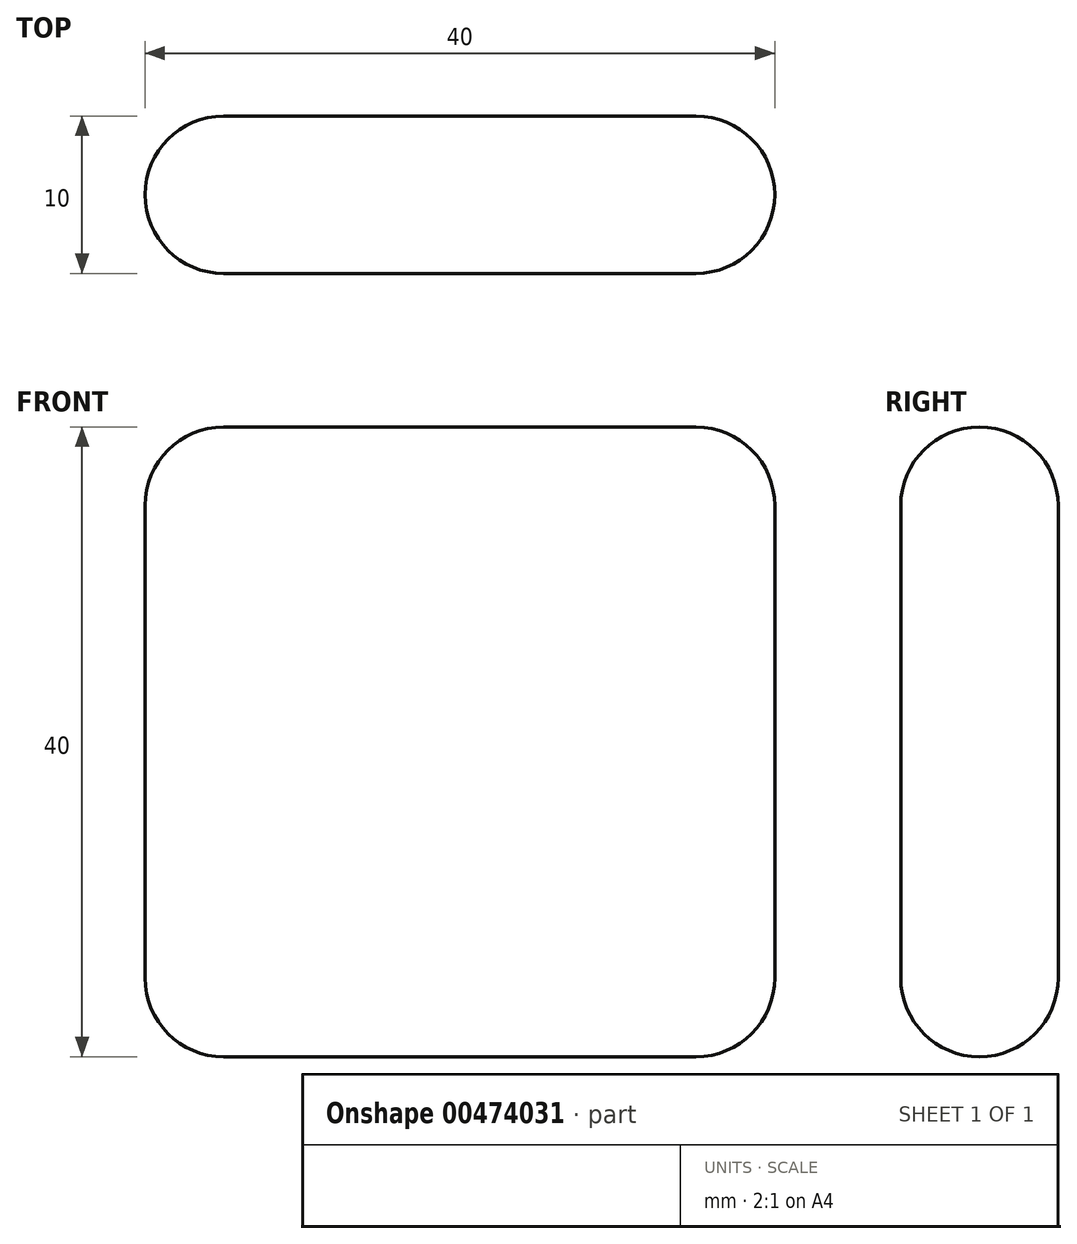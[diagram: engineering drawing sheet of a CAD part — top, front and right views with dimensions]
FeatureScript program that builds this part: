
annotation { "Feature Type Name" : "Feature", "Feature Type Description" : "" }
export const myFeature = defineFeature(function(context is Context, id is Id, definition is map)
    precondition{}
    {
        {
            var Q0;
            Q0=qCreatedBy(makeId("Front.planeOp"),FACE);
            var sketch = newSketch(context, id + "F0", { "sketchPlane" : qUnion([Q0])});
            skLineSegment(sketch, "E0.bottom", {"start": v(-19.76, 20.34) * mm, "end": v(20.24, 20.34) * mm});
            skLineSegment(sketch, "E0.top", {"start": v(-19.76, -19.66) * mm, "end": v(20.24, -19.66) * mm});
            skLineSegment(sketch, "E0.left", {"start": v(-19.76, 20.34) * mm, "end": v(-19.76, -19.66) * mm});
            skLineSegment(sketch, "E0.right", {"start": v(20.24, 20.34) * mm, "end": v(20.24, -19.66) * mm});
            skSolve(sketch);
        }
        {
            var Q0;
            Q0=makeQuery(id+"F0.imprint","IMPRINT",FACE,{"disambiguationData":[TD([[makeQuery(id+"F0.imprint","IMPRINT",EDGE,{"derivedFrom":sQuery(id+"F0.wireOp",EDGE,"E0.bottom")}),-1.0]])]});
            var sketch = newSketch(context, id + "F1", { "sketchPlane" : qUnion([Q0])});
            skSolve(sketch);
        }
        {
            var Q0;
            Q0=makeQuery(id+"F1.imprint","IMPRINT",FACE,{"disambiguationData":[TD([[makeQuery(id+"F1.imprint","IMPRINT",EDGE,{"derivedFrom":makeQuery(id+"F0.imprint","IMPRINT",EDGE,{"derivedFrom":sQuery(id+"F0.wireOp",EDGE,"E0.bottom")})}),-1.0]])]});
            var Q1;
            Q1=makeQuery(id+"F0.imprint","IMPRINT",FACE,{"disambiguationData":[TD([[makeQuery(id+"F0.imprint","IMPRINT",EDGE,{"derivedFrom":sQuery(id+"F0.wireOp",EDGE,"E0.bottom")}),-1.0]])]});
            extrude(context, id + "F2", {"entities" : qUnion([Q0, Q1]), "depth" : 10 * mm});
        }
        {
            var Q0;
            {var subQ0=sQuery(id+"F0.wireOp",EDGE,"E0.left");Q0=makeQuery(id+"F2.opExtrude","SWEPT_FACE",FACE,{"disambiguationData":[OSD([subQ0]),TDD([makeQuery(id+"F0.imprint","IMPRINT",EDGE,{"derivedFrom":subQ0})])]});}
            var Q1;
            {var subQ0=sQuery(id+"F0.wireOp",EDGE,"E0.right");Q1=makeQuery(id+"F2.opExtrude","SWEPT_FACE",FACE,{"disambiguationData":[OSD([subQ0]),TDD([makeQuery(id+"F0.imprint","IMPRINT",EDGE,{"derivedFrom":subQ0})])]});}
            var Q2;
            {var subQ0=sQuery(id+"F0.wireOp",EDGE,"E0.bottom");Q2=makeQuery(id+"F2.opExtrude","CAP_EDGE",EDGE,{"disambiguationData":[OSD([subQ0]),TDD([makeQuery(id+"F0.imprint","IMPRINT",EDGE,{"derivedFrom":subQ0})])],"isStart":true});}
            var Q3;
            {var subQ0=sQuery(id+"F0.wireOp",EDGE,"E0.bottom");Q3=makeQuery(id+"F2.opExtrude","CAP_EDGE",EDGE,{"disambiguationData":[OSD([subQ0]),TDD([makeQuery(id+"F0.imprint","IMPRINT",EDGE,{"derivedFrom":subQ0})])],"isStart":false});}
            var Q4;
            {var subQ0=sQuery(id+"F0.wireOp",EDGE,"E0.right");var subQ1=sQuery(id+"F0.wireOp",EDGE,"E0.bottom");Q4=makeQuery(id+"F2.opExtrude","SWEPT_EDGE",EDGE,{"disambiguationData":[OSD([subQ1,subQ0]),TDD([makeQuery(id+"F0.imprint","INTERSECT",VERTEX,{"derivedFrom":[subQ1,subQ0]})])]});}
            var Q5;
            {var subQ0=sQuery(id+"F0.wireOp",EDGE,"E0.right");var subQ1=sQuery(id+"F0.wireOp",EDGE,"E0.left");var subQ2=sQuery(id+"F0.wireOp",EDGE,"E0.top");var subQ3=sQuery(id+"F0.wireOp",EDGE,"E0.bottom");Q5=makeQuery(id+"F2.opExtrude","CAP_FACE",FACE,{"disambiguationData":[OSD([subQ3,subQ2,subQ1,subQ0]),TDD([makeQuery(id+"F0.imprint","IMPRINT",EDGE,{"derivedFrom":subQ3}),makeQuery(id+"F0.imprint","IMPRINT",EDGE,{"derivedFrom":subQ2}),makeQuery(id+"F0.imprint","IMPRINT",EDGE,{"derivedFrom":subQ1}),makeQuery(id+"F0.imprint","IMPRINT",EDGE,{"derivedFrom":subQ0})])],"isStart":true});}
            var Q6;
            {var subQ0=sQuery(id+"F0.wireOp",EDGE,"E0.left");var subQ1=sQuery(id+"F0.wireOp",EDGE,"E0.bottom");Q6=makeQuery(id+"F2.opExtrude","SWEPT_EDGE",EDGE,{"disambiguationData":[OSD([subQ1,subQ0]),TDD([makeQuery(id+"F0.imprint","INTERSECT",VERTEX,{"derivedFrom":[subQ1,subQ0]})])]});}
            var Q7;
            {var subQ0=sQuery(id+"F0.wireOp",EDGE,"E0.bottom");Q7=makeQuery(id+"F2.opExtrude","SWEPT_FACE",FACE,{"disambiguationData":[OSD([subQ0]),TDD([makeQuery(id+"F0.imprint","IMPRINT",EDGE,{"derivedFrom":subQ0})])]});}
            var Q8;
            {var subQ0=sQuery(id+"F0.wireOp",EDGE,"E0.right");var subQ1=sQuery(id+"F0.wireOp",EDGE,"E0.left");var subQ2=sQuery(id+"F0.wireOp",EDGE,"E0.top");var subQ3=sQuery(id+"F0.wireOp",EDGE,"E0.bottom");Q8=makeQuery(id+"F2.opExtrude","CAP_FACE",FACE,{"disambiguationData":[OSD([subQ3,subQ2,subQ1,subQ0]),TDD([makeQuery(id+"F0.imprint","IMPRINT",EDGE,{"derivedFrom":subQ3}),makeQuery(id+"F0.imprint","IMPRINT",EDGE,{"derivedFrom":subQ2}),makeQuery(id+"F0.imprint","IMPRINT",EDGE,{"derivedFrom":subQ1}),makeQuery(id+"F0.imprint","IMPRINT",EDGE,{"derivedFrom":subQ0})])],"isStart":false});}
            var Q9;
            {var subQ0=sQuery(id+"F0.wireOp",EDGE,"E0.right");var subQ1=sQuery(id+"F0.wireOp",EDGE,"E0.top");Q9=makeQuery(id+"F2.opExtrude","SWEPT_EDGE",EDGE,{"disambiguationData":[OSD([subQ1,subQ0]),TDD([makeQuery(id+"F0.imprint","INTERSECT",VERTEX,{"derivedFrom":[subQ1,subQ0]})])]});}
            var Q10;
            {var subQ0=sQuery(id+"F0.wireOp",EDGE,"E0.top");Q10=makeQuery(id+"F2.opExtrude","SWEPT_FACE",FACE,{"disambiguationData":[OSD([subQ0]),TDD([makeQuery(id+"F0.imprint","IMPRINT",EDGE,{"derivedFrom":subQ0})])]});}
            var Q11;
            {var subQ0=sQuery(id+"F0.wireOp",EDGE,"E0.top");Q11=makeQuery(id+"F2.opExtrude","CAP_EDGE",EDGE,{"disambiguationData":[OSD([subQ0]),TDD([makeQuery(id+"F0.imprint","IMPRINT",EDGE,{"derivedFrom":subQ0})])],"isStart":true});}
            var Q12;
            {var subQ0=sQuery(id+"F0.wireOp",EDGE,"E0.left");Q12=makeQuery(id+"F2.opExtrude","CAP_EDGE",EDGE,{"disambiguationData":[OSD([subQ0]),TDD([makeQuery(id+"F0.imprint","IMPRINT",EDGE,{"derivedFrom":subQ0})])],"isStart":true});}
            var Q13;
            {var subQ0=sQuery(id+"F0.wireOp",EDGE,"E0.right");Q13=makeQuery(id+"F2.opExtrude","CAP_EDGE",EDGE,{"disambiguationData":[OSD([subQ0]),TDD([makeQuery(id+"F0.imprint","IMPRINT",EDGE,{"derivedFrom":subQ0})])],"isStart":true});}
            var Q14;
            {var subQ0=sQuery(id+"F0.wireOp",EDGE,"E0.right");Q14=makeQuery(id+"F2.opExtrude","CAP_EDGE",EDGE,{"disambiguationData":[OSD([subQ0]),TDD([makeQuery(id+"F0.imprint","IMPRINT",EDGE,{"derivedFrom":subQ0})])],"isStart":false});}
            var Q15;
            {var subQ0=sQuery(id+"F0.wireOp",EDGE,"E0.right");var subQ1=sQuery(id+"F0.wireOp",EDGE,"E0.left");var subQ2=sQuery(id+"F0.wireOp",EDGE,"E0.top");var subQ3=sQuery(id+"F0.wireOp",EDGE,"E0.bottom");Q15=makeQuery(id+"F2.opExtrude","CAP_FACE",FACE,{"disambiguationData":[OSD([subQ3,subQ2,subQ1,subQ0]),TDD([makeQuery(id+"F1.imprint","IMPRINT",EDGE,{"derivedFrom":makeQuery(id+"F0.imprint","IMPRINT",EDGE,{"derivedFrom":subQ3})}),makeQuery(id+"F1.imprint","IMPRINT",EDGE,{"derivedFrom":makeQuery(id+"F0.imprint","IMPRINT",EDGE,{"derivedFrom":subQ2})}),makeQuery(id+"F1.imprint","IMPRINT",EDGE,{"derivedFrom":makeQuery(id+"F0.imprint","IMPRINT",EDGE,{"derivedFrom":subQ1})}),makeQuery(id+"F1.imprint","IMPRINT",EDGE,{"derivedFrom":makeQuery(id+"F0.imprint","IMPRINT",EDGE,{"derivedFrom":subQ0})})])],"isStart":true});}
            var Q16;
            {var subQ0=sQuery(id+"F0.wireOp",EDGE,"E0.left");var subQ1=sQuery(id+"F0.wireOp",EDGE,"E0.top");Q16=makeQuery(id+"F2.opExtrude","SWEPT_EDGE",EDGE,{"disambiguationData":[OSD([subQ1,subQ0]),TDD([makeQuery(id+"F0.imprint","INTERSECT",VERTEX,{"derivedFrom":[subQ1,subQ0]})])]});}
            var Q17;
            {var subQ0=sQuery(id+"F0.wireOp",EDGE,"E0.top");Q17=makeQuery(id+"F2.opExtrude","CAP_EDGE",EDGE,{"disambiguationData":[OSD([subQ0]),TDD([makeQuery(id+"F0.imprint","IMPRINT",EDGE,{"derivedFrom":subQ0})])],"isStart":false});}
            var Q18;
            {var subQ0=sQuery(id+"F0.wireOp",EDGE,"E0.right");var subQ1=sQuery(id+"F0.wireOp",EDGE,"E0.bottom");Q18=makeQuery(id+"F2.opExtrude","SWEPT_EDGE",EDGE,{"disambiguationData":[OSD([subQ1,subQ0]),TDD([makeQuery(id+"F1.imprint","INTERSECT",VERTEX,{"derivedFrom":[makeQuery(id+"F0.imprint","IMPRINT",EDGE,{"derivedFrom":subQ1}),makeQuery(id+"F0.imprint","IMPRINT",EDGE,{"derivedFrom":subQ0})]})])]});}
            var Q19;
            {var subQ0=sQuery(id+"F0.wireOp",EDGE,"E0.right");var subQ1=sQuery(id+"F0.wireOp",EDGE,"E0.top");Q19=makeQuery(id+"F2.opExtrude","SWEPT_EDGE",EDGE,{"disambiguationData":[OSD([subQ1,subQ0]),TDD([makeQuery(id+"F1.imprint","INTERSECT",VERTEX,{"derivedFrom":[makeQuery(id+"F0.imprint","IMPRINT",EDGE,{"derivedFrom":subQ1}),makeQuery(id+"F0.imprint","IMPRINT",EDGE,{"derivedFrom":subQ0})]})])]});}
            var Q20;
            {var subQ0=sQuery(id+"F0.wireOp",EDGE,"E0.bottom");Q20=makeQuery(id+"F2.opExtrude","SWEPT_FACE",FACE,{"disambiguationData":[OSD([subQ0]),TDD([makeQuery(id+"F1.imprint","IMPRINT",EDGE,{"derivedFrom":makeQuery(id+"F0.imprint","IMPRINT",EDGE,{"derivedFrom":subQ0})})])]});}
            var Q21;
            {var subQ0=sQuery(id+"F0.wireOp",EDGE,"E0.right");var subQ1=sQuery(id+"F0.wireOp",EDGE,"E0.left");var subQ2=sQuery(id+"F0.wireOp",EDGE,"E0.top");var subQ3=sQuery(id+"F0.wireOp",EDGE,"E0.bottom");Q21=makeQuery(id+"F2.opExtrude","CAP_FACE",FACE,{"disambiguationData":[OSD([subQ3,subQ2,subQ1,subQ0]),TDD([makeQuery(id+"F1.imprint","IMPRINT",EDGE,{"derivedFrom":makeQuery(id+"F0.imprint","IMPRINT",EDGE,{"derivedFrom":subQ3})}),makeQuery(id+"F1.imprint","IMPRINT",EDGE,{"derivedFrom":makeQuery(id+"F0.imprint","IMPRINT",EDGE,{"derivedFrom":subQ2})}),makeQuery(id+"F1.imprint","IMPRINT",EDGE,{"derivedFrom":makeQuery(id+"F0.imprint","IMPRINT",EDGE,{"derivedFrom":subQ1})}),makeQuery(id+"F1.imprint","IMPRINT",EDGE,{"derivedFrom":makeQuery(id+"F0.imprint","IMPRINT",EDGE,{"derivedFrom":subQ0})})])],"isStart":false});}
            var Q22;
            {var subQ0=sQuery(id+"F0.wireOp",EDGE,"E0.top");Q22=makeQuery(id+"F2.opExtrude","SWEPT_FACE",FACE,{"disambiguationData":[OSD([subQ0]),TDD([makeQuery(id+"F1.imprint","IMPRINT",EDGE,{"derivedFrom":makeQuery(id+"F0.imprint","IMPRINT",EDGE,{"derivedFrom":subQ0})})])]});}
            var Q23;
            {var subQ0=sQuery(id+"F0.wireOp",EDGE,"E0.left");Q23=makeQuery(id+"F2.opExtrude","SWEPT_FACE",FACE,{"disambiguationData":[OSD([subQ0]),TDD([makeQuery(id+"F1.imprint","IMPRINT",EDGE,{"derivedFrom":makeQuery(id+"F0.imprint","IMPRINT",EDGE,{"derivedFrom":subQ0})})])]});}
            var Q24;
            {var subQ0=sQuery(id+"F0.wireOp",EDGE,"E0.right");Q24=makeQuery(id+"F2.opExtrude","SWEPT_FACE",FACE,{"disambiguationData":[OSD([subQ0]),TDD([makeQuery(id+"F1.imprint","IMPRINT",EDGE,{"derivedFrom":makeQuery(id+"F0.imprint","IMPRINT",EDGE,{"derivedFrom":subQ0})})])]});}
            var Q25;
            {var subQ0=sQuery(id+"F0.wireOp",EDGE,"E0.left");var subQ1=sQuery(id+"F0.wireOp",EDGE,"E0.bottom");Q25=makeQuery(id+"F2.opExtrude","SWEPT_EDGE",EDGE,{"disambiguationData":[OSD([subQ1,subQ0]),TDD([makeQuery(id+"F1.imprint","INTERSECT",VERTEX,{"derivedFrom":[makeQuery(id+"F0.imprint","IMPRINT",EDGE,{"derivedFrom":subQ1}),makeQuery(id+"F0.imprint","IMPRINT",EDGE,{"derivedFrom":subQ0})]})])]});}
            var Q26;
            {var subQ0=sQuery(id+"F0.wireOp",EDGE,"E0.bottom");Q26=makeQuery(id+"F2.opExtrude","CAP_EDGE",EDGE,{"disambiguationData":[OSD([subQ0]),TDD([makeQuery(id+"F1.imprint","IMPRINT",EDGE,{"derivedFrom":makeQuery(id+"F0.imprint","IMPRINT",EDGE,{"derivedFrom":subQ0})})])],"isStart":true});}
            var Q27;
            {var subQ0=sQuery(id+"F0.wireOp",EDGE,"E0.bottom");Q27=makeQuery(id+"F2.opExtrude","CAP_EDGE",EDGE,{"disambiguationData":[OSD([subQ0]),TDD([makeQuery(id+"F1.imprint","IMPRINT",EDGE,{"derivedFrom":makeQuery(id+"F0.imprint","IMPRINT",EDGE,{"derivedFrom":subQ0})})])],"isStart":false});}
            var Q28;
            {var subQ0=sQuery(id+"F0.wireOp",EDGE,"E0.top");Q28=makeQuery(id+"F2.opExtrude","CAP_EDGE",EDGE,{"disambiguationData":[OSD([subQ0]),TDD([makeQuery(id+"F1.imprint","IMPRINT",EDGE,{"derivedFrom":makeQuery(id+"F0.imprint","IMPRINT",EDGE,{"derivedFrom":subQ0})})])],"isStart":true});}
            var Q29;
            {var subQ0=sQuery(id+"F0.wireOp",EDGE,"E0.left");Q29=makeQuery(id+"F2.opExtrude","CAP_EDGE",EDGE,{"disambiguationData":[OSD([subQ0]),TDD([makeQuery(id+"F1.imprint","IMPRINT",EDGE,{"derivedFrom":makeQuery(id+"F0.imprint","IMPRINT",EDGE,{"derivedFrom":subQ0})})])],"isStart":true});}
            var Q30;
            {var subQ0=sQuery(id+"F0.wireOp",EDGE,"E0.right");Q30=makeQuery(id+"F2.opExtrude","CAP_EDGE",EDGE,{"disambiguationData":[OSD([subQ0]),TDD([makeQuery(id+"F1.imprint","IMPRINT",EDGE,{"derivedFrom":makeQuery(id+"F0.imprint","IMPRINT",EDGE,{"derivedFrom":subQ0})})])],"isStart":true});}
            var Q31;
            {var subQ0=sQuery(id+"F0.wireOp",EDGE,"E0.right");Q31=makeQuery(id+"F2.opExtrude","CAP_EDGE",EDGE,{"disambiguationData":[OSD([subQ0]),TDD([makeQuery(id+"F1.imprint","IMPRINT",EDGE,{"derivedFrom":makeQuery(id+"F0.imprint","IMPRINT",EDGE,{"derivedFrom":subQ0})})])],"isStart":false});}
            var Q32;
            {var subQ0=sQuery(id+"F0.wireOp",EDGE,"E0.left");Q32=makeQuery(id+"F2.opExtrude","CAP_EDGE",EDGE,{"disambiguationData":[OSD([subQ0]),TDD([makeQuery(id+"F0.imprint","IMPRINT",EDGE,{"derivedFrom":subQ0})])],"isStart":false});}
            var Q33;
            {var subQ0=sQuery(id+"F0.wireOp",EDGE,"E0.left");var subQ1=sQuery(id+"F0.wireOp",EDGE,"E0.top");Q33=makeQuery(id+"F2.opExtrude","SWEPT_EDGE",EDGE,{"disambiguationData":[OSD([subQ1,subQ0]),TDD([makeQuery(id+"F1.imprint","INTERSECT",VERTEX,{"derivedFrom":[makeQuery(id+"F0.imprint","IMPRINT",EDGE,{"derivedFrom":subQ1}),makeQuery(id+"F0.imprint","IMPRINT",EDGE,{"derivedFrom":subQ0})]})])]});}
            var Q34;
            {var subQ0=sQuery(id+"F0.wireOp",EDGE,"E0.top");Q34=makeQuery(id+"F2.opExtrude","CAP_EDGE",EDGE,{"disambiguationData":[OSD([subQ0]),TDD([makeQuery(id+"F1.imprint","IMPRINT",EDGE,{"derivedFrom":makeQuery(id+"F0.imprint","IMPRINT",EDGE,{"derivedFrom":subQ0})})])],"isStart":false});}
            var Q35;
            {var subQ0=sQuery(id+"F0.wireOp",EDGE,"E0.left");Q35=makeQuery(id+"F2.opExtrude","CAP_EDGE",EDGE,{"disambiguationData":[OSD([subQ0]),TDD([makeQuery(id+"F1.imprint","IMPRINT",EDGE,{"derivedFrom":makeQuery(id+"F0.imprint","IMPRINT",EDGE,{"derivedFrom":subQ0})})])],"isStart":false});}
            fillet(context, id + "F3", {"entities" : qUnion([Q0, Q1, Q2, Q3, Q4, Q5, Q6, Q7, Q8, Q9, Q10, Q11, Q12, Q13, Q14, Q15, Q16, Q17, Q18, Q19, Q20, Q21, Q22, Q23, Q24, Q25, Q26, Q27, Q28, Q29, Q30, Q31, Q32, Q33, Q34, Q35]), "radius" : 5 * mm, "tangentPropagation" : true, "allowEdgeOverflow" : false});
        }
        {
            var Q0;
            {var subQ0=sQuery(id+"F0.wireOp",EDGE,"E0.right");var subQ1=sQuery(id+"F0.wireOp",EDGE,"E0.left");var subQ2=sQuery(id+"F0.wireOp",EDGE,"E0.top");var subQ3=sQuery(id+"F0.wireOp",EDGE,"E0.bottom");Q0=makeQuery(id+"F2.opExtrude","SWEPT_BODY",BODY,{"disambiguationData":[OSD([subQ3,subQ2,subQ1,subQ0]),TDD([makeQuery(id+"F1.imprint","IMPRINT",EDGE,{"derivedFrom":makeQuery(id+"F0.imprint","IMPRINT",EDGE,{"derivedFrom":subQ3})}),makeQuery(id+"F1.imprint","IMPRINT",EDGE,{"derivedFrom":makeQuery(id+"F0.imprint","IMPRINT",EDGE,{"derivedFrom":subQ2})}),makeQuery(id+"F1.imprint","IMPRINT",EDGE,{"derivedFrom":makeQuery(id+"F0.imprint","IMPRINT",EDGE,{"derivedFrom":subQ1})}),makeQuery(id+"F1.imprint","IMPRINT",EDGE,{"derivedFrom":makeQuery(id+"F0.imprint","IMPRINT",EDGE,{"derivedFrom":subQ0})})])]});}
            deleteBodies(context, id + "F4", {"entities" : qUnion([Q0])});
        }
    });
